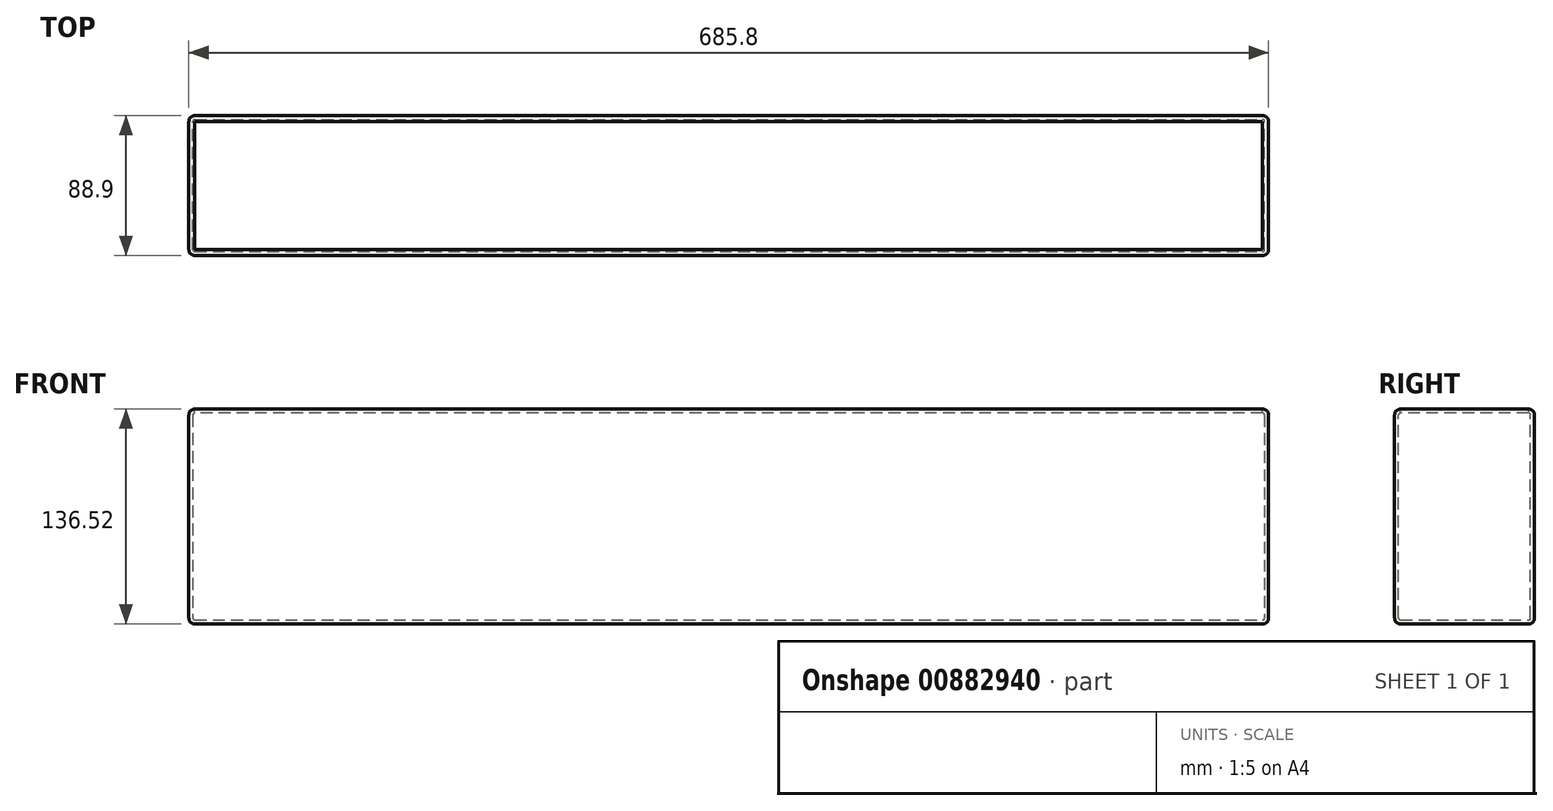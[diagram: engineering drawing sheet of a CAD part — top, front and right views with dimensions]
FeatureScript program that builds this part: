
annotation { "Feature Type Name" : "Feature", "Feature Type Description" : "" }
export const myFeature = defineFeature(function(context is Context, id is Id, definition is map)
    precondition{}
    {
        {
            var Q0;
            Q0=qCreatedBy(makeId("Front.planeOp"),FACE);
            var sketch = newSketch(context, id + "F0", { "sketchPlane" : qUnion([Q0])});
            skLineSegment(sketch, "E0.bottom", {"start": v(-342.9, 68.26) * mm, "end": v(342.9, 68.26) * mm});
            skLineSegment(sketch, "E0.top", {"start": v(-342.9, -68.26) * mm, "end": v(342.9, -68.26) * mm});
            skLineSegment(sketch, "E0.left", {"start": v(-342.9, 68.26) * mm, "end": v(-342.9, -68.26) * mm});
            skLineSegment(sketch, "E0.right", {"start": v(342.9, 68.26) * mm, "end": v(342.9, -68.26) * mm});
            skPoint(sketch, "E0.middle", {"position": v(0, 0) * mm});
            skSolve(sketch);
        }
        {
            var Q0;
            Q0=makeQuery(id+"F0.imprint","IMPRINT",FACE,{"disambiguationData":[TD([[makeQuery(id+"F0.imprint","IMPRINT",EDGE,{"derivedFrom":sQuery(id+"F0.wireOp",EDGE,"E0.bottom")}),-1.0]])]});
            extrude(context, id + "F1", {"entities" : qUnion([Q0]), "depth" : 88.9 * mm, "offsetDistance" : 25.4 * mm});
        }
        {
            var Q0;
            Q0=makeQuery(id+"F1.opExtrude","SWEPT_EDGE",EDGE,{"disambiguationData":[OSD([sQuery(id+"F0.wireOp",EDGE,"E0.bottom"),sQuery(id+"F0.wireOp",EDGE,"E0.left")])]});
            var Q1;
            Q1=makeQuery(id+"F1.opExtrude","SWEPT_FACE",FACE,{"disambiguationData":[OSD([sQuery(id+"F0.wireOp",EDGE,"E0.bottom")])]});
            var Q2;
            Q2=makeQuery(id+"F1.opExtrude","SWEPT_EDGE",EDGE,{"disambiguationData":[OSD([sQuery(id+"F0.wireOp",EDGE,"E0.bottom"),sQuery(id+"F0.wireOp",EDGE,"E0.right")])]});
            var Q3;
            Q3=makeQuery(id+"F1.opExtrude","CAP_FACE",FACE,{"disambiguationData":[OSD([sQuery(id+"F0.wireOp",EDGE,"E0.bottom"),sQuery(id+"F0.wireOp",EDGE,"E0.top"),sQuery(id+"F0.wireOp",EDGE,"E0.left"),sQuery(id+"F0.wireOp",EDGE,"E0.right")])],"isStart":true});
            var Q4;
            Q4=makeQuery(id+"F1.opExtrude","SWEPT_EDGE",EDGE,{"disambiguationData":[OSD([sQuery(id+"F0.wireOp",EDGE,"E0.top"),sQuery(id+"F0.wireOp",EDGE,"E0.left")])]});
            var Q5;
            Q5=makeQuery(id+"F1.opExtrude","CAP_FACE",FACE,{"disambiguationData":[OSD([sQuery(id+"F0.wireOp",EDGE,"E0.bottom"),sQuery(id+"F0.wireOp",EDGE,"E0.top"),sQuery(id+"F0.wireOp",EDGE,"E0.left"),sQuery(id+"F0.wireOp",EDGE,"E0.right")])],"isStart":false});
            var Q6;
            Q6=makeQuery(id+"F1.opExtrude","SWEPT_FACE",FACE,{"disambiguationData":[OSD([sQuery(id+"F0.wireOp",EDGE,"E0.top")])]});
            var Q7;
            Q7=makeQuery(id+"F1.opExtrude","CAP_EDGE",EDGE,{"disambiguationData":[OSD([sQuery(id+"F0.wireOp",EDGE,"E0.bottom")])],"isStart":true});
            var Q8;
            Q8=makeQuery(id+"F1.opExtrude","SWEPT_FACE",FACE,{"disambiguationData":[OSD([sQuery(id+"F0.wireOp",EDGE,"E0.left")])]});
            var Q9;
            Q9=makeQuery(id+"F1.opExtrude","CAP_EDGE",EDGE,{"disambiguationData":[OSD([sQuery(id+"F0.wireOp",EDGE,"E0.bottom")])],"isStart":false});
            var Q10;
            Q10=makeQuery(id+"F1.opExtrude","CAP_EDGE",EDGE,{"disambiguationData":[OSD([sQuery(id+"F0.wireOp",EDGE,"E0.top")])],"isStart":false});
            var Q11;
            Q11=makeQuery(id+"F1.opExtrude","SWEPT_EDGE",EDGE,{"disambiguationData":[OSD([sQuery(id+"F0.wireOp",EDGE,"E0.top"),sQuery(id+"F0.wireOp",EDGE,"E0.right")])]});
            var Q12;
            Q12=makeQuery(id+"F1.opExtrude","SWEPT_FACE",FACE,{"disambiguationData":[OSD([sQuery(id+"F0.wireOp",EDGE,"E0.right")])]});
            var Q13;
            Q13=makeQuery(id+"F1.opExtrude","CAP_EDGE",EDGE,{"disambiguationData":[OSD([sQuery(id+"F0.wireOp",EDGE,"E0.top")])],"isStart":true});
            var Q14;
            Q14=makeQuery(id+"F1.opExtrude","CAP_EDGE",EDGE,{"disambiguationData":[OSD([sQuery(id+"F0.wireOp",EDGE,"E0.left")])],"isStart":true});
            var Q15;
            Q15=makeQuery(id+"F1.opExtrude","CAP_EDGE",EDGE,{"disambiguationData":[OSD([sQuery(id+"F0.wireOp",EDGE,"E0.left")])],"isStart":false});
            var Q16;
            Q16=makeQuery(id+"F1.opExtrude","CAP_EDGE",EDGE,{"disambiguationData":[OSD([sQuery(id+"F0.wireOp",EDGE,"E0.right")])],"isStart":true});
            var Q17;
            Q17=makeQuery(id+"F1.opExtrude","CAP_EDGE",EDGE,{"disambiguationData":[OSD([sQuery(id+"F0.wireOp",EDGE,"E0.right")])],"isStart":false});
            fillet(context, id + "F2", {"entities" : qUnion([Q0, Q1, Q2, Q3, Q4, Q5, Q6, Q7, Q8, Q9, Q10, Q11, Q12, Q13, Q14, Q15, Q16, Q17]), "radius" : 3.8 * mm, "tangentPropagation" : true, "allowEdgeOverflow" : false});
        }
        {
            var Q0;
            Q0=makeQuery(id+"F1.opExtrude","SWEPT_FACE",FACE,{"disambiguationData":[OSD([sQuery(id+"F0.wireOp",EDGE,"E0.bottom")])]});
            shell(context, id + "F3", {"entities" : qUnion([Q0]), "thickness" : 2.54 * mm});
        }
    });
